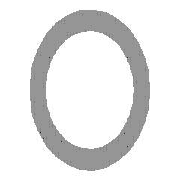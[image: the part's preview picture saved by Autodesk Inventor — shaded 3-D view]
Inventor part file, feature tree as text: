
AUTODESK INVENTOR PART (.ipt)
format: ipt  version: 2021 (Build 250183000, 183)  size: 160,256 bytes
history: native  units: mm (DEFAULTED — no unit token found)
features: other x10, sketch x4, extrude x2, plane x1
ambient origin geometry x8: Origin, YZ Plane, XZ Plane, XY Plane, X Axis, Y Axis, Z Axis, Center Point
bodies: Solid1 (feature_tree)
feature tree (17):
  parser-record x1  (decoder bookkeeping rows leaked as tree rows — omitted from the tree; the rows remain in map.json)
  other  "Driven Length"
  other  "Plano inicial"
  other  "Plano final"
  extrude  "Cuerpo"  Depth=4.8514mm
  extrude  "Extrusión2"  TaperAngle=0.0deg  [1 undecoded]
  sketch  "Boceto"  dims[d6=90.0deg d7=550.0mm d84=5.0mm d85=40.0mm d86=0.0mm d203=5.0mm d204=0.0mm d205=5.0mm d206=0.0mm]
  sketch  "Sketch3"  dims[d0=42.164mm d1=4.8514mm]
  plane  "Work Plane3"
  sketch  "Sketch4"  dims[d2=528.33989mm d3=0.0mm d4=-0.0mm]
  sketch  "Boceto5"  dims[d5=550.0mm]
  other  "Sup146"
  other  "Sup147"
  other  "Sólido50"
  other  "Sup145"
  other  "Superficie de contorno97"
  other  "Superficie de contorno98"
note: 1 required parameter value undecoded (feature->parameter linkage not recoverable at this tier; creation-order binding heuristic only, values carry confidence <= 0.55)
